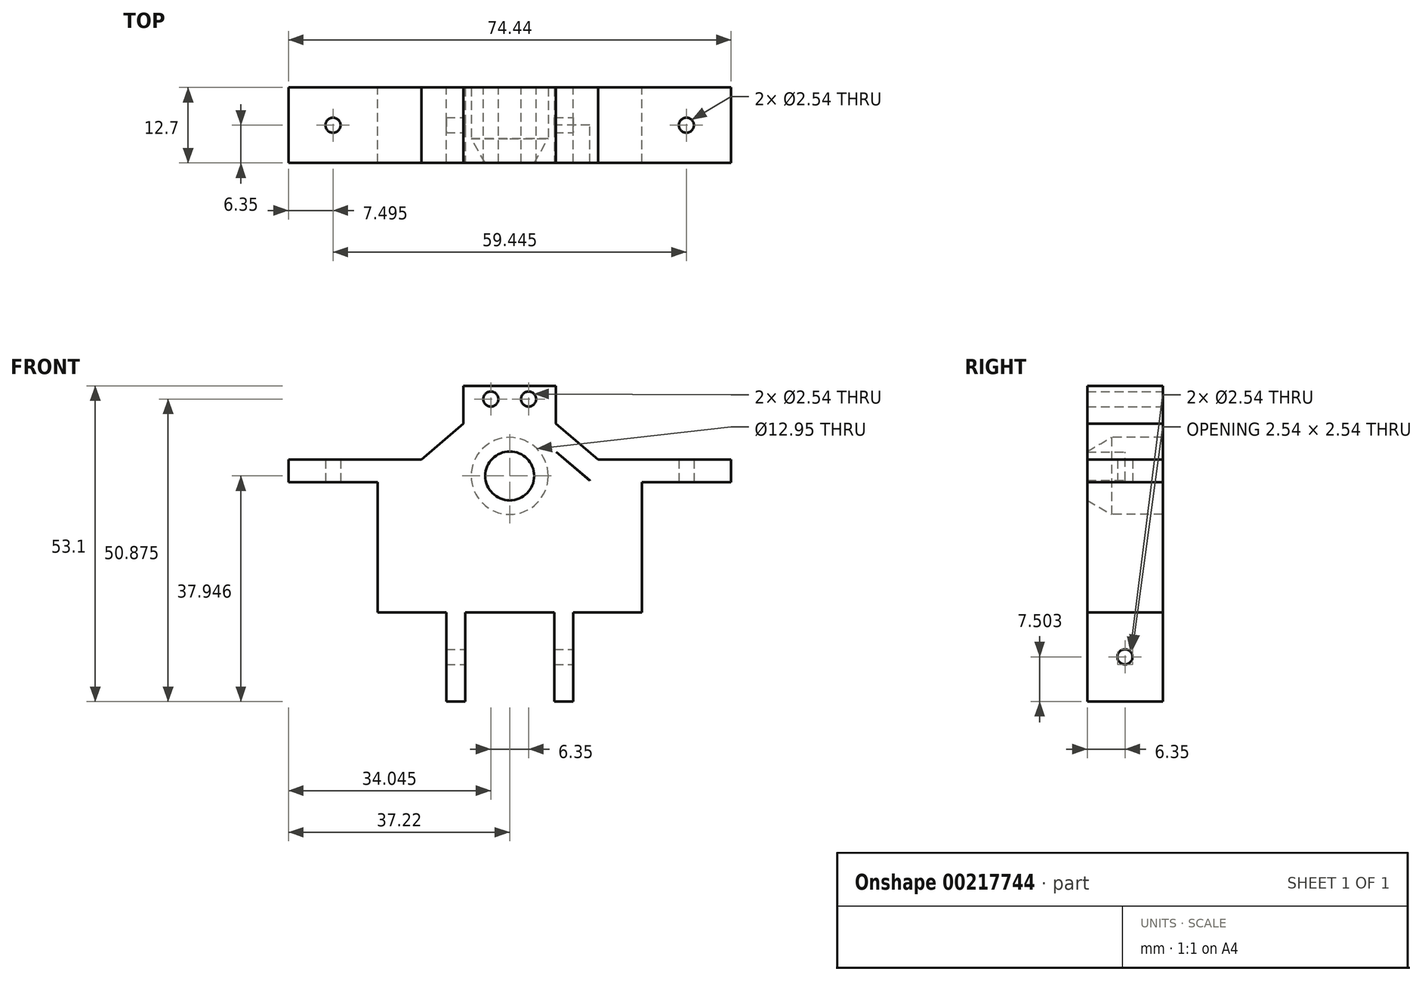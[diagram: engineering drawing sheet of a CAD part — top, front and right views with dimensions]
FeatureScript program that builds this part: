
annotation { "Feature Type Name" : "Feature", "Feature Type Description" : "" }
export const myFeature = defineFeature(function(context is Context, id is Id, definition is map)
    precondition{}
    {
        {
            var Q0;
            Q0=qCreatedBy(makeId("Front.planeOp"),FACE);
            var sketch = newSketch(context, id + "F0", { "sketchPlane" : qUnion([Q0])});
            skLineSegment(sketch, "E0", {"start": v(0, 0.13) * mm, "end": v(7.5, 0.13) * mm});
            skLineSegment(sketch, "E1", {"start": v(-22.22, 19.5) * mm, "end": v(-22.22, 4.52) * mm});
            skLineSegment(sketch, "E2", {"start": v(-7.5, 0.13) * mm, "end": v(0, 0.13) * mm});
            skArc(sketch, "E3", {"start": v(-13.47, 22.3) * mm, "mid": v(-14.04, 9.06) * mm, "end": v(-1.65, 13.77) * mm});
            skArc(sketch, "E4.MirrorC", {"start": v(13.47, 22.3) * mm, "mid": v(14.05, 9.06) * mm, "end": v(1.65, 13.75) * mm});
            skArc(sketch, "E5", {"start": v(1.65, 13.75) * mm, "mid": v(0, 14.71) * mm, "end": v(-1.65, 13.77) * mm});
            skLineSegment(sketch, "E6", {"start": v(-22.22, 19.5) * mm, "end": v(-22.22, 0.13) * mm});
            skLineSegment(sketch, "E7.MirrorCS", {"start": v(22.22, 19.5) * mm, "end": v(22.22, 0.13) * mm});
            skLineSegment(sketch, "E8", {"start": v(0, 0.13) * mm, "end": v(-22.22, 0.13) * mm});
            skLineSegment(sketch, "E9", {"start": v(0, 0.13) * mm, "end": v(22.22, 0.13) * mm});
            skPoint(sketch, "E10.orphan", {"position": v(-22.22, 0) * mm});
            skLineSegment(sketch, "E11", {"start": v(-3.18, 27.12) * mm, "end": v(-3.18, 30.3) * mm});
            skLineSegment(sketch, "E12", {"start": v(3.17, 30.3) * mm, "end": v(3.17, 27.12) * mm});
            skLineSegment(sketch, "E13", {"start": v(3.17, 27.12) * mm, "end": v(3.17, 27.12) * mm});
            skLineSegment(sketch, "E14", {"start": v(-22.22, 19.5) * mm, "end": v(-7.77, 31.88) * mm});
            skLineSegment(sketch, "E15", {"start": v(-3.18, 27.12) * mm, "end": v(-7.84, 27.12) * mm});
            skLineSegment(sketch, "E16", {"start": v(-13.47, 22.3) * mm, "end": v(-7.84, 27.12) * mm});
            skLineSegment(sketch, "E17.MirrorCS", {"start": v(3.17, 27.12) * mm, "end": v(7.84, 27.12) * mm});
            skLineSegment(sketch, "E18.MirrorCS", {"start": v(13.46, 22.3) * mm, "end": v(7.84, 27.12) * mm});
            skLineSegment(sketch, "E19.MirrorCS", {"start": v(3.17, 30.3) * mm, "end": v(3.18, 30.3) * mm});
            skLineSegment(sketch, "E20.MirrorCS", {"start": v(22.22, 19.5) * mm, "end": v(7.77, 31.88) * mm});
            skPoint(sketch, "E21.end.orphan", {"position": v(-9.63, 30.3) * mm});
            skPoint(sketch, "E22.orphan", {"position": v(9.62, 30.3) * mm});
            skPoint(sketch, "E23.start.orphan", {"position": v(0, 27.12) * mm});
            skLineSegment(sketch, "E24", {"start": v(13.47, 22.3) * mm, "end": v(7.84, 27.12) * mm});
            skLineSegment(sketch, "E25", {"start": v(3.17, 27.12) * mm, "end": v(3.17, 30.3) * mm});
            skLineSegment(sketch, "E26", {"start": v(-3.18, 30.3) * mm, "end": v(-3.18, 27.12) * mm});
            skLineSegment(sketch, "E27", {"start": v(-7.84, 27.12) * mm, "end": v(-13.47, 22.3) * mm});
            skArc(sketch, "E28", {"start": v(1.65, 13.75) * mm, "mid": v(14.06, 9.07) * mm, "end": v(13.45, 22.31) * mm});
            skPoint(sketch, "E29.startSnap0", {"position": v(0, 30.3) * mm});
            skPoint(sketch, "E30.orphan", {"position": v(22.22, 2.54) * mm});
            skLineSegment(sketch, "E31", {"start": v(3.17, 30.3) * mm, "end": v(3.17, 33.47) * mm});
            skLineSegment(sketch, "E32", {"start": v(3.17, 33.47) * mm, "end": v(-3.18, 33.47) * mm});
            skLineSegment(sketch, "E33", {"start": v(-3.18, 33.47) * mm, "end": v(-3.18, 30.3) * mm});
            skLineSegment(sketch, "E34", {"start": v(-7.77, 31.88) * mm, "end": v(-7.77, 38.23) * mm});
            skLineSegment(sketch, "E35", {"start": v(7.77, 31.88) * mm, "end": v(7.77, 38.23) * mm});
            skLineSegment(sketch, "E36", {"start": v(7.77, 38.23) * mm, "end": v(-7.77, 38.23) * mm});
            skCircle(sketch, "E37", {"center": v(-9.4, 15.5) * mm, "radius": 7.94 * mm});
            skCircle(sketch, "E38", {"center": v(9.4, 15.5) * mm, "radius": 7.94 * mm});
            skCircle(sketch, "E39", {"center": v(0, 23.08) * mm, "radius": 3.97 * mm});
            skLineSegment(sketch, "E40", {"start": v(-22.22, 0.13) * mm, "end": v(-22.22, 25.81) * mm});
            skLineSegment(sketch, "E41", {"start": v(-22.22, 25.81) * mm, "end": v(-17.42, 25.81) * mm});
            skLineSegment(sketch, "E42", {"start": v(-17.42, 25.81) * mm, "end": v(-12.1, 25.81) * mm});
            skLineSegment(sketch, "E43", {"start": v(0, 12.81) * mm, "end": v(0, 7.67) * mm});
            skLineSegment(sketch, "E44.MirrorCS", {"start": v(22.22, 0.13) * mm, "end": v(22.22, 25.81) * mm});
            skLineSegment(sketch, "E45.MirrorCS", {"start": v(22.22, 25.81) * mm, "end": v(17.42, 25.81) * mm});
            skLineSegment(sketch, "E46.MirrorCS", {"start": v(17.42, 25.81) * mm, "end": v(12.09, 25.81) * mm});
            skCircle(sketch, "E47", {"center": v(3.17, 36) * mm, "radius": 1.27 * mm});
            skCircle(sketch, "E48", {"center": v(-3.18, 36) * mm, "radius": 1.27 * mm});
            skSolve(sketch);
        }
        {
            var Q0;
            Q0=qSketchRegion(id+"F0",true);
            var Q1;
            {var subQ0=sQuery(id+"F0.wireOp",EDGE,"E38");var subQ1=makeQuery(id+"F0.imprint","INTERSECT",VERTEX,{"derivedFrom":[sQuery(id+"F0.wireOp",EDGE,"E24"),subQ0]});Q1=makeQuery(id+"F0.imprint","IMPRINT",FACE,{"disambiguationData":[TD([[makeQuery(id+"F0.imprint","IMPRINT",EDGE,{"disambiguationData":[TD([[subQ1,-1.0]])],"derivedFrom":subQ0}),1.0]])]});}
            var Q2;
            {var subQ0=sQuery(id+"F0.wireOp",EDGE,"E37");var subQ1=makeQuery(id+"F0.imprint","INTERSECT",VERTEX,{"derivedFrom":[sQuery(id+"F0.wireOp",EDGE,"E27"),subQ0]});Q2=makeQuery(id+"F0.imprint","IMPRINT",FACE,{"disambiguationData":[TD([[makeQuery(id+"F0.imprint","IMPRINT",EDGE,{"disambiguationData":[TD([[subQ1,-1.0]])],"derivedFrom":subQ0}),1.0]])]});}
            var Q3;
            Q3=makeQuery(id+"F0.imprint","IMPRINT",FACE,{"disambiguationData":[TD([[makeQuery(id+"F0.imprint","IMPRINT",EDGE,{"derivedFrom":sQuery(id+"F0.wireOp",EDGE,"E15")}),1.0]])]});
            extrude(context, id + "F1", {"entities" : qUnion([Q0, Q1, Q2, Q3]), "depth" : 6.35 * mm});
        }
        {
            var Q0;
            Q0=makeQuery(id+"F1.opExtrude","CAP_FACE",FACE,{"disambiguationData":[OSD([sQuery(id+"F0.wireOp",EDGE,"E6"),sQuery(id+"F0.wireOp",EDGE,"E7.MirrorCS"),sQuery(id+"F0.wireOp",EDGE,"E8"),sQuery(id+"F0.wireOp",EDGE,"E9"),sQuery(id+"F0.wireOp",EDGE,"E14"),sQuery(id+"F0.wireOp",EDGE,"E18.MirrorCS"),sQuery(id+"F0.wireOp",EDGE,"E20.MirrorCS"),sQuery(id+"F0.wireOp",EDGE,"E24"),sQuery(id+"F0.wireOp",EDGE,"E34"),sQuery(id+"F0.wireOp",EDGE,"E35"),sQuery(id+"F0.wireOp",EDGE,"E36"),sQuery(id+"F0.wireOp",EDGE,"E38"),sQuery(id+"F0.wireOp",EDGE,"E39")])],"isStart":true});
            var sketch = newSketch(context, id + "F2", { "sketchPlane" : qUnion([Q0])});
            skCircle(sketch, "E49", {"center": v(0, 23.08) * mm, "radius": 6.48 * mm});
            skLineSegment(sketch, "E50", {"start": v(-22.22, 0.13) * mm, "end": v(22.22, 0.13) * mm});
            skLineSegment(sketch, "E51", {"start": v(7.77, 31.88) * mm, "end": v(7.77, 31.88) * mm});
            skLineSegment(sketch, "E52", {"start": v(7.77, 31.88) * mm, "end": v(7.77, 38.23) * mm});
            skLineSegment(sketch, "E53", {"start": v(7.77, 38.23) * mm, "end": v(-7.77, 38.23) * mm});
            skLineSegment(sketch, "E54", {"start": v(-7.77, 38.23) * mm, "end": v(-7.77, 31.88) * mm});
            skLineSegment(sketch, "E55", {"start": v(-7.77, 31.88) * mm, "end": v(-7.77, 31.88) * mm});
            skLineSegment(sketch, "E56", {"start": v(22.22, 0.13) * mm, "end": v(22.22, 25.81) * mm});
            skLineSegment(sketch, "E57", {"start": v(-22.22, 0.13) * mm, "end": v(-22.22, 25.81) * mm});
            skLineSegment(sketch, "E58", {"start": v(-22.22, 25.81) * mm, "end": v(-14.86, 25.81) * mm});
            skLineSegment(sketch, "E59", {"start": v(-14.86, 25.81) * mm, "end": v(-7.77, 31.88) * mm});
            skLineSegment(sketch, "E60", {"start": v(22.22, 25.81) * mm, "end": v(14.86, 25.81) * mm});
            skLineSegment(sketch, "E61", {"start": v(14.86, 25.81) * mm, "end": v(7.77, 31.88) * mm});
            skCircle(sketch, "E62", {"center": v(-3.17, 36) * mm, "radius": 1.27 * mm});
            skCircle(sketch, "E63", {"center": v(3.18, 36) * mm, "radius": 1.27 * mm});
            skSolve(sketch);
        }
        {
            var Q0;
            Q0=qSketchRegion(id+"F2",true);
            extrude(context, id + "F3", {"entities" : qUnion([Q0]), "operationType" : NewBodyOperationType.ADD, "depth" : 6.35 * mm});
        }
        {
            var Q0;
            Q0=makeQuery(id+"F1.opExtrude","CAP_EDGE",EDGE,{"disambiguationData":[OSD([sQuery(id+"F0.wireOp",EDGE,"E39")])],"isStart":true});
            chamfer(context, id + "F4", {"entities" : qUnion([Q0]), "chamferType" : ChamferType.OFFSET_ANGLE, "width" : 3.8 * mm, "oppositeDirection" : false, "angle" : 60 * degree, "tangentPropagation" : true});
        }
        {
            var Q0;
            Q0=makeQuery(id+"F3.boolean.opBoolean","MERGE",FACE,{"derivedFrom":[makeQuery(id+"F1.opExtrude","SWEPT_FACE",FACE,{"disambiguationData":[OSD([sQuery(id+"F0.wireOp",EDGE,"E40")])]}),makeQuery(id+"F3.opExtrude","SWEPT_FACE",FACE,{"disambiguationData":[OSD([sQuery(id+"F2.wireOp",EDGE,"E56")])]})]});
            var sketch = newSketch(context, id + "F5", { "sketchPlane" : qUnion([Q0])});
            skLineSegment(sketch, "E64", {"start": v(6.35, 0.13) * mm, "end": v(6.35, 22) * mm});
            skLineSegment(sketch, "E65", {"start": v(6.35, 22) * mm, "end": v(-6.35, 22) * mm});
            skLineSegment(sketch, "E66", {"start": v(-6.35, 22) * mm, "end": v(-6.35, 25.81) * mm});
            skLineSegment(sketch, "E67", {"start": v(-6.35, 25.81) * mm, "end": v(6.35, 25.81) * mm});
            skLineSegment(sketch, "E68", {"start": v(6.35, 25.81) * mm, "end": v(6.35, 22) * mm});
            skSolve(sketch);
        }
        {
            var Q0;
            Q0=qSketchRegion(id+"F5",true);
            extrude(context, id + "F6", {"entities" : qUnion([Q0]), "operationType" : NewBodyOperationType.ADD, "depth" : 15 * mm});
        }
        {
            var Q0;
            Q0=makeQuery(id+"F6.opExtrude","SWEPT_FACE",FACE,{"disambiguationData":[OSD([sQuery(id+"F5.wireOp",EDGE,"E65")])]});
            var sketch = newSketch(context, id + "F7", { "sketchPlane" : qUnion([Q0])});
            skLineSegment(sketch, "E69", {"start": v(-37.22, -6.35) * mm, "end": v(-22.22, 6.35) * mm});
            skCircle(sketch, "E70", {"center": v(-29.72, 0) * mm, "radius": 1.27 * mm});
            skSolve(sketch);
        }
        {
            var Q0;
            Q0=qSketchRegion(id+"F7",true);
            extrude(context, id + "F8", {"entities" : qUnion([Q0]), "operationType" : NewBodyOperationType.REMOVE, "oppositeDirection" : true, "depth" : 25.4 * mm});
        }
        {
            var Q0;
            Q0=makeQuery(id+"F3.boolean.opBoolean","MERGE",FACE,{"derivedFrom":[makeQuery(id+"F1.opExtrude","SWEPT_FACE",FACE,{"disambiguationData":[OSD([sQuery(id+"F0.wireOp",EDGE,"E44.MirrorCS")])]}),makeQuery(id+"F3.opExtrude","SWEPT_FACE",FACE,{"disambiguationData":[OSD([sQuery(id+"F2.wireOp",EDGE,"E57")])]})]});
            var sketch = newSketch(context, id + "F9", { "sketchPlane" : qUnion([Q0])});
            skLineSegment(sketch, "E71", {"start": v(-6.35, 0.13) * mm, "end": v(-6.35, 25.81) * mm});
            skLineSegment(sketch, "E72", {"start": v(-6.35, 25.81) * mm, "end": v(6.35, 25.81) * mm});
            skLineSegment(sketch, "E73", {"start": v(6.35, 25.81) * mm, "end": v(6.35, 22) * mm});
            skLineSegment(sketch, "E74", {"start": v(6.35, 22) * mm, "end": v(-6.35, 22) * mm});
            skSolve(sketch);
        }
        {
            var Q0;
            Q0=qSketchRegion(id+"F9",true);
            extrude(context, id + "F10", {"entities" : qUnion([Q0]), "operationType" : NewBodyOperationType.ADD, "depth" : 15 * mm});
        }
        {
            var Q0;
            Q0=makeQuery(id+"F10.opExtrude","SWEPT_FACE",FACE,{"disambiguationData":[OSD([sQuery(id+"F9.wireOp",EDGE,"E74")])]});
            var sketch = newSketch(context, id + "F11", { "sketchPlane" : qUnion([Q0])});
            skLineSegment(sketch, "E75", {"start": v(37.22, 6.35) * mm, "end": v(22.22, -6.35) * mm});
            skCircle(sketch, "E76", {"center": v(29.72, 0) * mm, "radius": 1.27 * mm});
            skSolve(sketch);
        }
        {
            var Q0;
            Q0=qSketchRegion(id+"F11",true);
            extrude(context, id + "F12", {"entities" : qUnion([Q0]), "operationType" : NewBodyOperationType.REMOVE, "oppositeDirection" : true, "depth" : 25.4 * mm});
        }
        {
            var Q0;
            Q0=makeQuery(id+"F3.boolean.opBoolean","MERGE",FACE,{"derivedFrom":[makeQuery(id+"F1.opExtrude","SWEPT_FACE",FACE,{"disambiguationData":[OSD([sQuery(id+"F0.wireOp",EDGE,"E8"),sQuery(id+"F0.wireOp",EDGE,"E9")])]}),makeQuery(id+"F3.opExtrude","SWEPT_FACE",FACE,{"disambiguationData":[OSD([sQuery(id+"F2.wireOp",EDGE,"E50")])]})]});
            var sketch = newSketch(context, id + "F13", { "sketchPlane" : qUnion([Q0])});
            skLineSegment(sketch, "E77", {"start": v(0, -6.35) * mm, "end": v(7.5, -6.35) * mm});
            skLineSegment(sketch, "E78", {"start": v(0, -6.35) * mm, "end": v(-7.5, -6.35) * mm});
            skLineSegment(sketch, "E79", {"start": v(-7.5, -6.35) * mm, "end": v(-7.5, 6.35) * mm});
            skLineSegment(sketch, "E80", {"start": v(-7.5, 6.35) * mm, "end": v(-10.67, 6.35) * mm});
            skLineSegment(sketch, "E81", {"start": v(-10.67, 6.35) * mm, "end": v(-10.67, -6.35) * mm});
            skLineSegment(sketch, "E82", {"start": v(-10.67, -6.35) * mm, "end": v(-7.5, -6.35) * mm});
            skLineSegment(sketch, "E83", {"start": v(7.5, -6.35) * mm, "end": v(7.5, 6.35) * mm});
            skLineSegment(sketch, "E84", {"start": v(7.5, 6.35) * mm, "end": v(10.67, 6.35) * mm});
            skLineSegment(sketch, "E85", {"start": v(10.67, 6.35) * mm, "end": v(10.67, -6.35) * mm});
            skLineSegment(sketch, "E86", {"start": v(10.67, -6.35) * mm, "end": v(7.5, -6.35) * mm});
            skSolve(sketch);
        }
        {
            var Q0;
            Q0=qSketchRegion(id+"F13",true);
            extrude(context, id + "F14", {"entities" : qUnion([Q0]), "operationType" : NewBodyOperationType.ADD, "depth" : 15 * mm});
        }
        {
            var Q0;
            Q0=makeQuery(id+"F14.opExtrude","SWEPT_FACE",FACE,{"disambiguationData":[OSD([sQuery(id+"F13.wireOp",EDGE,"E85")])]});
            var sketch = newSketch(context, id + "F15", { "sketchPlane" : qUnion([Q0])});
            skLineSegment(sketch, "E87", {"start": v(-6.35, 0.13) * mm, "end": v(6.35, -14.87) * mm});
            skCircle(sketch, "E88", {"center": v(0, -7.37) * mm, "radius": 1.27 * mm});
            skSolve(sketch);
        }
        {
            var Q0;
            Q0=qSketchRegion(id+"F15",true);
            extrude(context, id + "F16", {"entities" : qUnion([Q0]), "operationType" : NewBodyOperationType.REMOVE, "oppositeDirection" : true, "depth" : 25.4 * mm});
        }
    });
